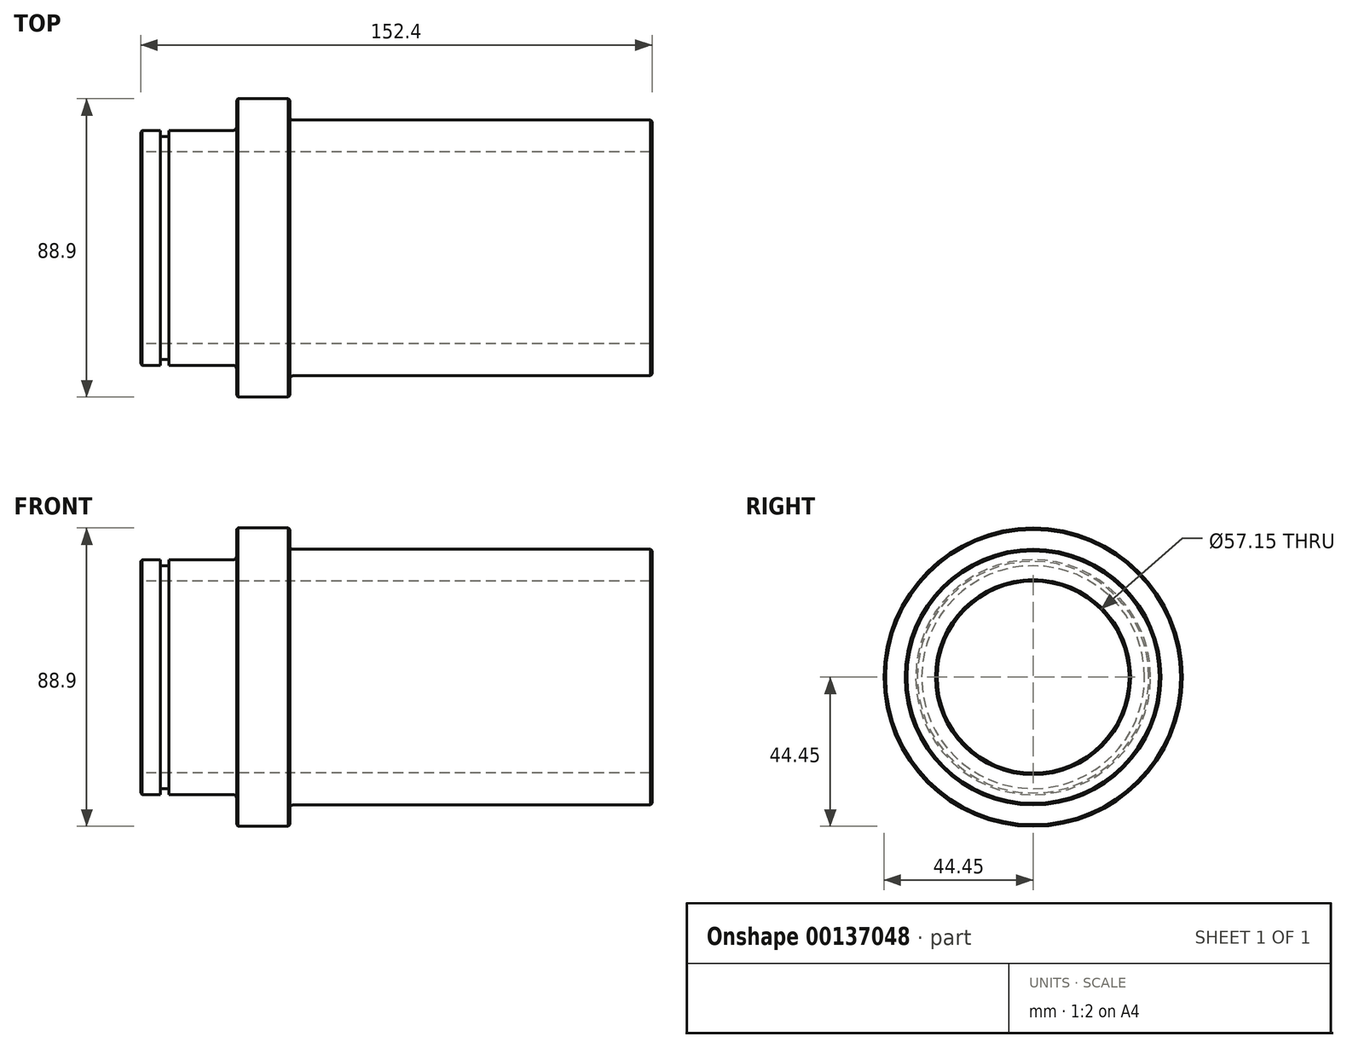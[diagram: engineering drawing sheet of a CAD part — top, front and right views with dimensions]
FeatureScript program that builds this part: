
annotation { "Feature Type Name" : "Feature", "Feature Type Description" : "" }
export const myFeature = defineFeature(function(context is Context, id is Id, definition is map)
    precondition{}
    {
        {
            var Q0;
            Q0=qCreatedBy(makeId("Front.planeOp"),FACE);
            var sketch = newSketch(context, id + "F0", { "sketchPlane" : qUnion([Q0])});
            skLineSegment(sketch, "E0", {"start": v(-44.45, 28.57) * mm, "end": v(-44.45, 35) * mm});
            skLineSegment(sketch, "E1", {"start": v(-44.45, 35) * mm, "end": v(-38.5, 35) * mm});
            skLineSegment(sketch, "E2", {"start": v(-38.5, 35) * mm, "end": v(-38.5, 33.2) * mm});
            skLineSegment(sketch, "E3", {"start": v(-38.5, 33.2) * mm, "end": v(-35.95, 33.2) * mm});
            skLineSegment(sketch, "E4", {"start": v(-35.95, 33.2) * mm, "end": v(-35.95, 35) * mm});
            skLineSegment(sketch, "E5", {"start": v(-35.95, 35) * mm, "end": v(-15.88, 35) * mm});
            skLineSegment(sketch, "E6", {"start": v(-15.87, 35) * mm, "end": v(-15.88, 44.45) * mm});
            skLineSegment(sketch, "E7", {"start": v(-15.88, 44.45) * mm, "end": v(0, 44.45) * mm});
            skLineSegment(sketch, "E8", {"start": v(0, 44.45) * mm, "end": v(0, 38.1) * mm});
            skLineSegment(sketch, "E9", {"start": v(0, 38.1) * mm, "end": v(107.95, 38.1) * mm});
            skLineSegment(sketch, "E10", {"start": v(107.95, 38.1) * mm, "end": v(107.95, 28.58) * mm});
            skLineSegment(sketch, "E11", {"start": v(107.95, 28.58) * mm, "end": v(-44.45, 28.57) * mm});
            skLineSegment(sketch, "E12", {"start": v(0, 0) * mm, "end": v(38.55, 0) * mm, "construction": true});
            skSolve(sketch);
        }
        {
            var Q0;
            Q0=makeQuery(id+"F0.imprint","IMPRINT",FACE,{"disambiguationData":[TD([[makeQuery(id+"F0.imprint","IMPRINT",EDGE,{"derivedFrom":sQuery(id+"F0.wireOp",EDGE,"E0")}),-1.0]])]});
            var Q1;
            Q1=sQuery(id+"F0.wireOp",EDGE,"E12");
            revolve(context, id + "F1", {"entities" : qUnion([Q0]), "axis" : qUnion([Q1]), "revolveType" : RevolveType.FULL});
        }
        {
            var Q0;
            Q0=makeQuery(id+"F1.opRevolve","SWEPT_EDGE",EDGE,{"disambiguationData":[OSD([sQuery(id+"F0.wireOp",EDGE,"E9"),sQuery(id+"F0.wireOp",EDGE,"E10")])]});
            var Q1;
            Q1=makeQuery(id+"F1.opRevolve","SWEPT_EDGE",EDGE,{"disambiguationData":[OSD([sQuery(id+"F0.wireOp",EDGE,"E10"),sQuery(id+"F0.wireOp",EDGE,"E11")])]});
            var Q2;
            Q2=makeQuery(id+"F1.opRevolve","SWEPT_EDGE",EDGE,{"disambiguationData":[OSD([sQuery(id+"F0.wireOp",EDGE,"E0"),sQuery(id+"F0.wireOp",EDGE,"E11")])]});
            var Q3;
            Q3=makeQuery(id+"F1.opRevolve","SWEPT_EDGE",EDGE,{"disambiguationData":[OSD([sQuery(id+"F0.wireOp",EDGE,"E0"),sQuery(id+"F0.wireOp",EDGE,"E1")])]});
            var Q4;
            Q4=makeQuery(id+"F1.opRevolve","SWEPT_EDGE",EDGE,{"disambiguationData":[OSD([sQuery(id+"F0.wireOp",EDGE,"E6"),sQuery(id+"F0.wireOp",EDGE,"E7")])]});
            var Q5;
            Q5=makeQuery(id+"F1.opRevolve","SWEPT_EDGE",EDGE,{"disambiguationData":[OSD([sQuery(id+"F0.wireOp",EDGE,"E7"),sQuery(id+"F0.wireOp",EDGE,"E8")])]});
            chamfer(context, id + "F2", {"entities" : qUnion([Q0, Q1, Q2, Q3, Q4, Q5]), "width" : 0.5 * mm, "tangentPropagation" : true});
        }
        {
            var Q0;
            Q0=makeQuery(id+"F1.opRevolve","SWEPT_EDGE",EDGE,{"disambiguationData":[OSD([sQuery(id+"F0.wireOp",EDGE,"E5"),sQuery(id+"F0.wireOp",EDGE,"E6")])]});
            var Q1;
            Q1=makeQuery(id+"F1.opRevolve","SWEPT_EDGE",EDGE,{"disambiguationData":[OSD([sQuery(id+"F0.wireOp",EDGE,"E8"),sQuery(id+"F0.wireOp",EDGE,"E9")])]});
            fillet(context, id + "F3", {"entities" : qUnion([Q0, Q1]), "radius" : 1 * mm, "tangentPropagation" : true, "allowEdgeOverflow" : false});
        }
    });
